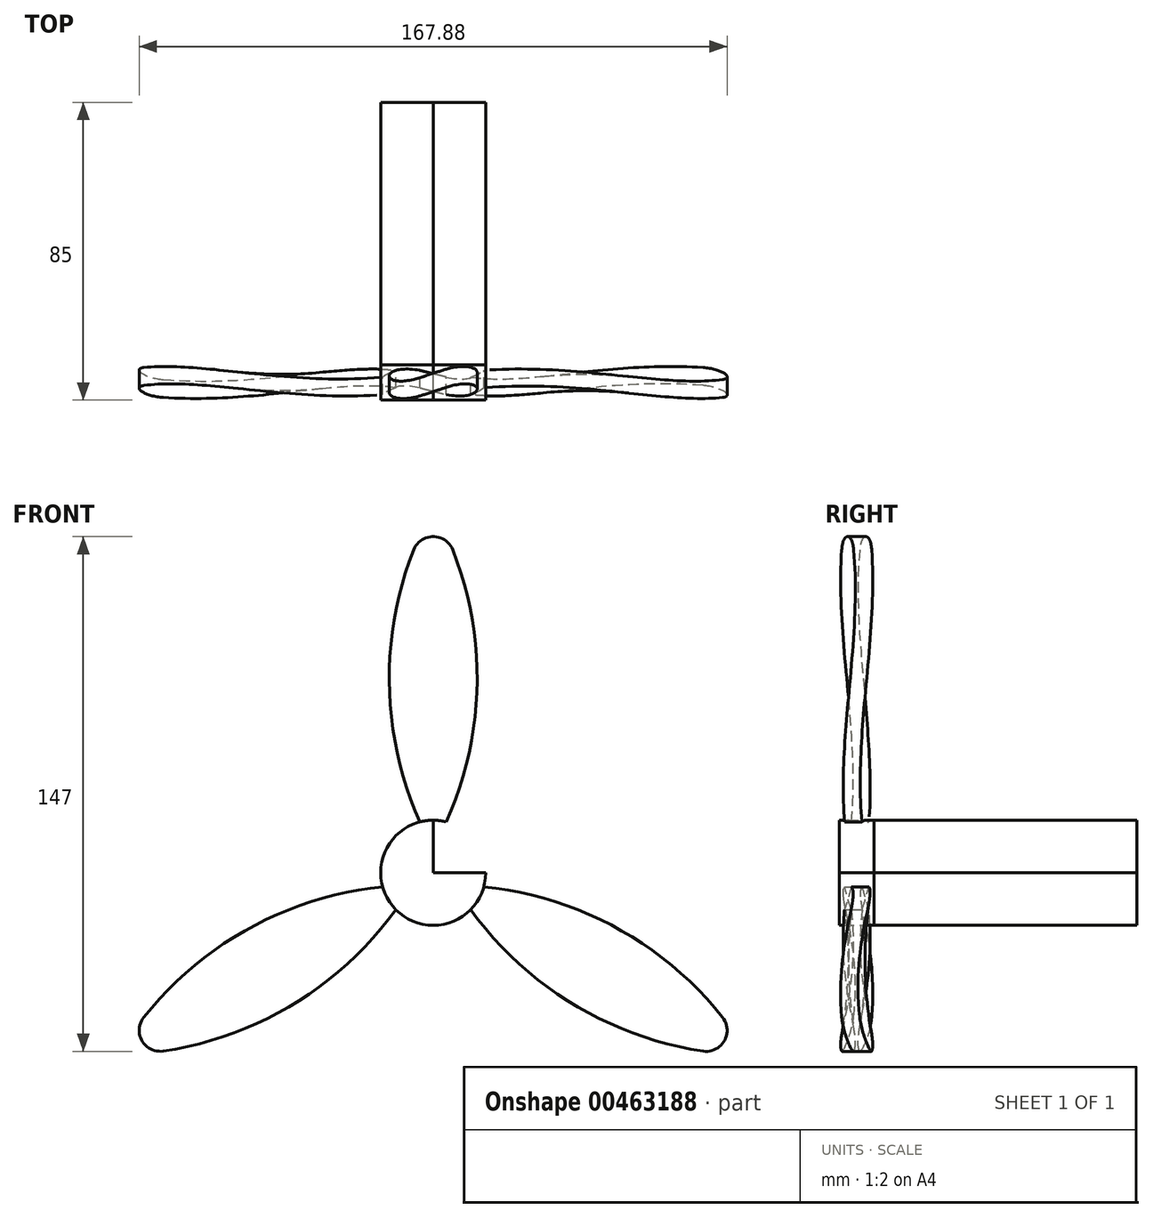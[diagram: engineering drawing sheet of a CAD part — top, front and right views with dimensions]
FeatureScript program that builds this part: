
annotation { "Feature Type Name" : "Feature", "Feature Type Description" : "" }
export const myFeature = defineFeature(function(context is Context, id is Id, definition is map)
    precondition{}
    {
        {
            var Q0;
            Q0=qCreatedBy(makeId("Top.planeOp"),FACE);
            cPlane(context, id + "F0", {"entities" : qUnion([Q0]), "cplaneType" : CPlaneType.OFFSET, "offset" : 100 * mm, "width" : 150 * mm, "height" : 150 * mm});
        }
        {
            var Q0;
            Q0=qCreatedBy(makeId("Top.planeOp"),FACE);
            var sketch = newSketch(context, id + "F1", { "sketchPlane" : qUnion([Q0])});
            skPoint(sketch, "E0.middle", {"position": v(0, 0) * mm});
            skLineSegment(sketch, "E1", {"start": v(-8.8, 0) * mm, "end": v(8.8, 0) * mm, "construction": true});
            skLineSegment(sketch, "E2", {"start": v(0, 7.7) * mm, "end": v(0, -5.94) * mm, "construction": true});
            skLineSegment(sketch, "E3", {"start": v(-22.64, 10.9) * mm, "end": v(24.35, -6.2) * mm});
            skLineSegment(sketch, "E4", {"start": v(24.35, -6.2) * mm, "end": v(22.64, -10.9) * mm});
            skLineSegment(sketch, "E5", {"start": v(22.64, -10.9) * mm, "end": v(-24.35, 6.2) * mm});
            skLineSegment(sketch, "E6", {"start": v(-24.35, 6.2) * mm, "end": v(-22.64, 10.9) * mm});
            skLineSegment(sketch, "E7", {"start": v(-23.5, 8.55) * mm, "end": v(23.5, -8.55) * mm, "construction": true});
            skLineSegment(sketch, "E8", {"start": v(0.86, 2.35) * mm, "end": v(-0.86, -2.35) * mm, "construction": true});
            skSolve(sketch);
        }
        {
            var Q0;
            Q0=qCreatedBy(id+"F0.planeOp",FACE);
            var sketch = newSketch(context, id + "F2", { "sketchPlane" : qUnion([Q0])});
            skLineSegment(sketch, "E9", {"start": v(0, 23.15) * mm, "end": v(0, -28.63) * mm, "construction": true});
            skLineSegment(sketch, "E10", {"start": v(-30.74, 0) * mm, "end": v(34.4, 0) * mm, "construction": true});
            skLineSegment(sketch, "E11", {"start": v(-24.35, -6.2) * mm, "end": v(22.64, 10.9) * mm});
            skLineSegment(sketch, "E12", {"start": v(22.64, 10.9) * mm, "end": v(24.35, 6.2) * mm});
            skLineSegment(sketch, "E13", {"start": v(24.35, 6.2) * mm, "end": v(-22.64, -10.9) * mm});
            skLineSegment(sketch, "E14", {"start": v(-22.64, -10.9) * mm, "end": v(-24.35, -6.2) * mm});
            skLineSegment(sketch, "E15", {"start": v(23.5, 8.55) * mm, "end": v(-23.5, -8.55) * mm, "construction": true});
            skLineSegment(sketch, "E16", {"start": v(-0.86, 2.35) * mm, "end": v(0.86, -2.35) * mm, "construction": true});
            skSolve(sketch);
        }
        {
            var Q0;
            Q0 = qSketchRegion(id + "F1", true);
            var Q1;
            Q1 = qSketchRegion(id + "F2", true);
            loft(context, id + "F3", {"sheetProfilesArray" : [{ "sheetProfileEntities" : qUnion([Q0]) }, { "sheetProfileEntities" : qUnion([Q1]) }]});
        }
        {
            var Q0;
            Q0=qCreatedBy(makeId("Front.planeOp"),FACE);
            var sketch = newSketch(context, id + "F4", { "sketchPlane" : qUnion([Q0])});
            skLineSegment(sketch, "E17", {"start": v(0, 105.19) * mm, "end": v(0, -5.12) * mm, "construction": true});
            skArc(sketch, "E18", {"start": v(0, 7) * mm, "mid": v(12.34, 48.98) * mm, "end": v(5.58, 92.2) * mm});
            skArc(sketch, "E19", {"start": v(5.58, 92.2) * mm, "mid": v(3.38, 94.96) * mm, "end": v(0, 96) * mm});
            skArc(sketch, "E20.MirrorCS", {"start": v(-5.58, 92.2) * mm, "mid": v(-3.38, 94.96) * mm, "end": v(0, 96) * mm});
            skArc(sketch, "E21.MirrorCS", {"start": v(0, 7) * mm, "mid": v(-12.34, 48.98) * mm, "end": v(-5.58, 92.2) * mm});
            skSolve(sketch);
        }
        {
            var Q0;
            Q0 = qSketchRegion(id + "F4", true);
            extrude(context, id + "F5", {"entities" : qUnion([Q0]), "operationType" : NewBodyOperationType.INTERSECT, "endBound" : BoundingType.SYMMETRIC, "depth" : 20 * mm});
        }
        {
            var Q0;
            Q0=qCreatedBy(makeId("Front.planeOp"),FACE);
            var sketch = newSketch(context, id + "F6", { "sketchPlane" : qUnion([Q0])});
            skCircle(sketch, "E22", {"center": v(0, 0) * mm, "radius": 15 * mm});
            skSolve(sketch);
        }
        {
            var Q0;
            Q0 = qSketchRegion(id + "F6", true);
            extrude(context, id + "F7", {"entities" : qUnion([Q0]), "operationType" : NewBodyOperationType.ADD, "endBound" : BoundingType.SYMMETRIC, "depth" : 10 * mm});
        }
        {
            var Q0;
            Q0=makeQuery(id+"F3.opLoft","SWEPT_BODY",BODY,{"disambiguationData":[OSD([makeQuery(id+"F1.imprint","IMPRINT",FACE,{"disambiguationData":[TD([[makeQuery(id+"F1.imprint","IMPRINT",EDGE,{"derivedFrom":sQuery(id+"F1.wireOp",EDGE,"E3")}),-1.0]])]}),makeQuery(id+"F2.imprint","IMPRINT",FACE,{"disambiguationData":[TD([[makeQuery(id+"F2.imprint","IMPRINT",EDGE,{"derivedFrom":sQuery(id+"F2.wireOp",EDGE,"E11")}),-1.0]])]})])]});
            var Q1;
            Q1=makeQuery(id+"F7.opExtrude","SWEPT_FACE",FACE,{"disambiguationData":[OSD([sQuery(id+"F6.wireOp",EDGE,"E22")])]});
            circularPattern(context, id + "F8", {"entities" : qUnion([Q0]), "axis" : qUnion([Q1]), "angle" : 360 * degree, "instanceCount" : 3, "equalSpace" : true});
        }
        {
            var Q0;
            Q0=makeQuery(id+"F8.opPattern","COPY",FACE,{"derivedFrom":makeQuery(id+"F7.opExtrude","CAP_FACE",FACE,{"disambiguationData":[OSD([sQuery(id+"F6.wireOp",EDGE,"E22")])],"isStart":true}),"instanceName":"1"});
            extrude(context, id + "F9", {"entities" : qUnion([Q0]), "depth" : 25 * mm, "offsetDistance" : 25 * mm});
        }
        {
            var Q0;
            Q0=makeQuery(id+"F9.opExtrude","CAP_FACE",FACE,{"disambiguationData":[OSD([sQuery(id+"F6.wireOp",EDGE,"E22")])],"isStart":false});
            var sketch = newSketch(context, id + "F10", { "sketchPlane" : qUnion([Q0])});
            skLineSegment(sketch, "E23.bottom", {"start": v(0, 0) * mm, "end": v(12.87, 0) * mm});
            skLineSegment(sketch, "E23.top", {"start": v(0, 23.05) * mm, "end": v(12.87, 23.05) * mm});
            skLineSegment(sketch, "E23.left", {"start": v(0, 0) * mm, "end": v(0, 23.05) * mm});
            skLineSegment(sketch, "E23.right", {"start": v(12.87, 0) * mm, "end": v(12.87, 23.05) * mm});
            skSolve(sketch);
        }
        {
            var Q0;
            {var subQ0=sQuery(id+"F10.wireOp",EDGE,"E23.bottom");Q0=makeQuery(id+"F10.imprint","IMPRINT",FACE,{"disambiguationData":[TD([[makeQuery(id+"F10.imprint","IMPRINT",EDGE,{"derivedFrom":subQ0}),1.0]])]});}
            var Q1;
            {var subQ0=sQuery(id+"F10.wireOp",EDGE,"E23.bottom");Q1=makeQuery(id+"F10.imprint","IMPRINT",FACE,{"disambiguationData":[TD([[makeQuery(id+"F10.imprint","IMPRINT",EDGE,{"derivedFrom":subQ0}),-1.0]])]});}
            extrude(context, id + "F11", {"entities" : qUnion([Q0, Q1]), "operationType" : NewBodyOperationType.ADD, "depth" : 50 * mm, "offsetDistance" : 25 * mm});
        }
        {
            var Q0;
            Q0=makeQuery(id+"F11.opExtrude","CAP_FACE",FACE,{"disambiguationData":[OSD([sQuery(id+"F6.wireOp",EDGE,"E22")])],"isStart":false});
            var sketch = newSketch(context, id + "F12", { "sketchPlane" : qUnion([Q0])});
            skLineSegment(sketch, "E24.bottom", {"start": v(0, 0) * mm, "end": v(-123.56, 0) * mm});
            skLineSegment(sketch, "E24.top", {"start": v(0, 72.04) * mm, "end": v(-123.56, 72.04) * mm});
            skLineSegment(sketch, "E24.left", {"start": v(0, 0) * mm, "end": v(0, 72.04) * mm});
            skLineSegment(sketch, "E24.right", {"start": v(-123.56, 0) * mm, "end": v(-123.56, 72.04) * mm});
            skSolve(sketch);
        }
        {
            var Q0;
            {var subQ0=sQuery(id+"F12.wireOp",EDGE,"E24.left");var subQ1=sQuery(id+"F12.wireOp",EDGE,"E24.bottom");var subQ2=makeQuery(id+"F12.imprint","INTERSECT",VERTEX,{"derivedFrom":[subQ1,subQ0]});Q0=makeQuery(id+"F12.imprint","IMPRINT",FACE,{"disambiguationData":[TD([[makeQuery(id+"F12.imprint","IMPRINT",EDGE,{"disambiguationData":[TD([[subQ2,-1.0]])],"derivedFrom":subQ1}),-1.0]])]});}
            extrude(context, id + "F13", {"entities" : qUnion([Q0]), "operationType" : NewBodyOperationType.REMOVE, "endBound" : BoundingType.THROUGH_ALL, "oppositeDirection" : true, "depth" : 25 * mm, "offsetDistance" : 25 * mm});
        }
    });
